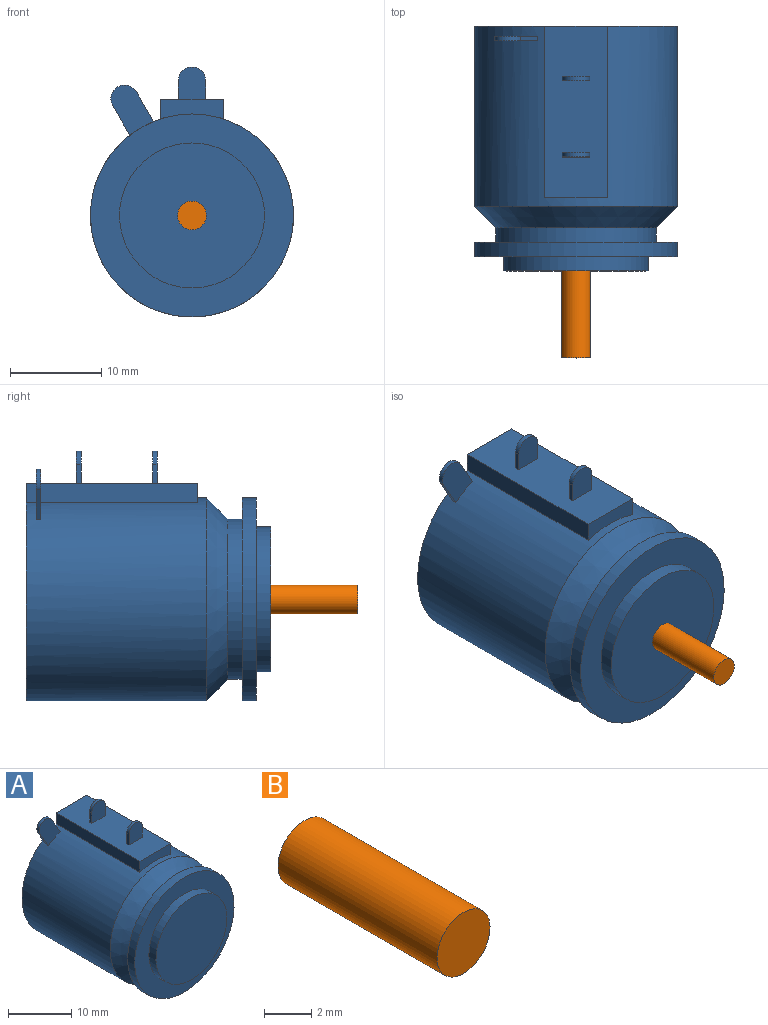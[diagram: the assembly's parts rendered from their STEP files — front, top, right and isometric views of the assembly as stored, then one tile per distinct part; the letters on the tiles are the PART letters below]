
ASSEMBLY  parts=2 mates=1
PART A: 28 faces, bbox 22.2x26.8x27.4 mm
  f0: plane 15.87x15.87mm, normal (0,-1,0), area 197.9mm2, adj f7
  f1: plane 23.81x22.23mm, normal (0,1,0), area 400.1mm2, adj f2,f9,f10,f11
  f2: cylinder r=11.11mm len=22.23mm, axis (0,1,0), area 1245mm2, adj f1,f8,f9,f10,f12,f21,f22,f23
  f3: cylinder r=8.76mm len=17.53mm, axis (0,1,0), area 86.7mm2, adj f4,f8
  f4: plane 22.23x22.23mm, normal (0,1,0), area 146.7mm2, adj f3,f5
  f5: cylinder r=11.11mm len=22.23mm, axis (0,1,0), area 110mm2, adj f4,f6
  f6: plane 22.23x22.23mm, normal (0,-1,0), area 190.1mm2, adj f5,f7
  f7: cylinder r=7.94mm len=15.87mm, axis (0,1,0), area 78.5mm2, adj f0,f6
  f8: cone r=11.11mm half-angle=45deg, axis (0,1,0), area 207.5mm2, adj f2,f3
  f9: plane 18.72x2.13mm, normal (1,0,0), area 39.9mm2, adj f1,f2,f11,f12
  f10: plane 18.72x2.13mm, normal (-1,0,0), area 39.9mm2, adj f1,f2,f11,f12
  f11: plane 18.72x6.86mm, normal (0,0,1), area 125.4mm2, adj f1,f9,f10,f12,f13,f14,f15,f16
  f12: plane 6.86x2.13mm, normal (0,-1,0), area 12.1mm2, adj f2,f9,f10,f11
  f13: plane 3.56x3mm, normal (0,-1,0), area 9.7mm2, adj f11,f15,f16,f27
  f14: plane 3.56x3mm, normal (0,1,0), area 9.7mm2, adj f11,f15,f16,f27
  f15: plane 2.06x0.5mm, normal (1,0,0), area 1mm2, adj f11,f13,f14,f27
  f16: plane 2.06x0.5mm, normal (-1,0,0), area 1mm2, adj f11,f13,f14,f27
  f17: plane 3.56x3mm, normal (0,-1,0), area 9.7mm2, adj f11,f19,f20,f26
  f18: plane 3.56x3mm, normal (0,1,0), area 9.7mm2, adj f11,f19,f20,f26
  f19: plane 2.06x0.5mm, normal (1,0,0), area 1mm2, adj f11,f17,f18,f26
  f20: plane 2.06x0.5mm, normal (-1,0,0), area 1mm2, adj f11,f17,f18,f26
  f21: plane 3.24x1.87mm, normal (0.87,0,0.5), area 1.9mm2, adj f2,f23,f24,f25
  f22: plane 3.24x1.87mm, normal (-0.87,0,-0.5), area 1.9mm2, adj f2,f23,f24,f25
  f23: plane 5.49x4.67mm, normal (0,-1,0), area 14.6mm2, adj f2,f21,f22,f25
  f24: plane 5.49x4.67mm, normal (0,1,0), area 14.6mm2, adj f2,f21,f22,f25
  f25: cylinder r=1.5mm len=2.8mm, axis (0,1,0), area 2.4mm2, adj f21,f22,f23,f24
  f26: cylinder r=1.5mm len=3mm, axis (0,1,0), area 2.4mm2, adj f17,f18,f19,f20
  f27: cylinder r=1.5mm len=3mm, axis (0,1,0), area 2.4mm2, adj f13,f14,f15,f16
PART B: 3 faces, bbox 3.2x9.5x3.2 mm
  f0: cylinder r=1.58mm len=9.53mm, axis (0,1,0), area 94.9mm2, adj f1,f2
  f1: plane 3.17x3.17mm, normal (0,-1,0), area 7.9mm2, adj f0
  f2: plane 3.17x3.17mm, normal (0,1,0), area 7.9mm2, adj f0
PLACE A t=(-12.13,-7,0)mm
PLACE B t=(-12.13,-7,0)mm
MATE revolute A.f2 <-> B.f0  axis (0,-1,0) through (-12.13,-7,0)mm
